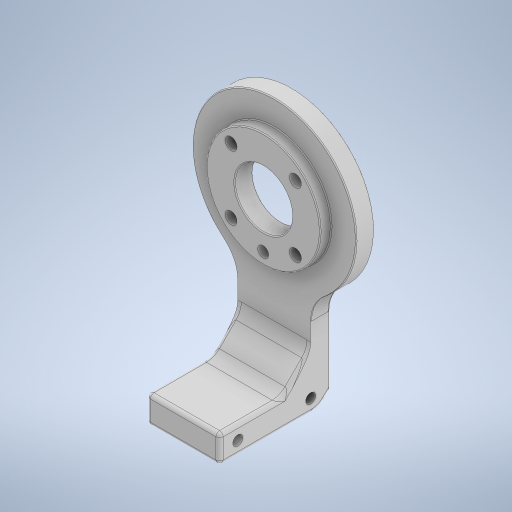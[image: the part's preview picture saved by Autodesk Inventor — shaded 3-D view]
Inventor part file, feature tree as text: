
AUTODESK INVENTOR PART (.ipt)
format: ipt  version: 2023 (Build 270158000, 158)  size: 553,984 bytes
history: native  units: mm
features: sketch x5, fillet x4, hole x3, other x2, extrude x2, chamfer x2, pattern_circular x1
ambient origin geometry x8: Origin, YZ Plane, XZ Plane, XY Plane, X Axis, Y Axis, Z Axis, Center Point
bodies: Body1 (feature_tree)
feature tree (19):
  other  "Těleso1"
  other  "Rotace1"
  fillet  "Zaoblení1"  Radius=45.0mm
  sketch  "Náčrt3"
  hole  "Díra1"  [1 undecoded]
  hole  "Díra2"  [1 undecoded]
  pattern_circular  "Kruhové pole1"  [2 undecoded]
  extrude  "Vysunutí4"  TaperAngle=90.0deg  [1 undecoded]
  extrude  "Vysunutí5"  Depth=0.5mm
  chamfer  "Zkosení2"  Distance=50.0mm
  chamfer  "Zkosení3"  Angle=45.0deg  [1 undecoded]
  fillet  "Zaoblení6"  Radius=40.0mm
  fillet  "Zaoblení9"  Radius=10.0mm
  fillet  "Zaoblení10"  Radius=10.0mm
  hole  "Díra3"  [1 undecoded]
  sketch  "Náčrt2"
  sketch  "Náčrt8"
  sketch  "Náčrt9"
  sketch  "Náčrt10"
note: 7 required parameter values undecoded (feature->parameter linkage not recoverable at this tier; creation-order binding heuristic only, values carry confidence <= 0.55)
